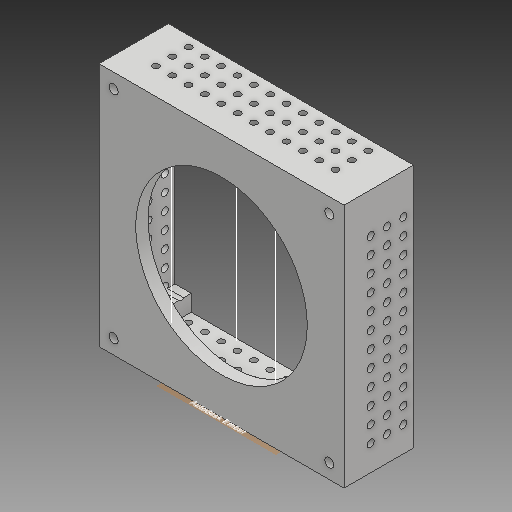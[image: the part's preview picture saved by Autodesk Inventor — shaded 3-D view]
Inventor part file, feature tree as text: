
AUTODESK INVENTOR PART (.ipt)
format: ipt  version: 2018 (Build 220112000, 112)  size: 539,648 bytes
history: native  units: mm
features: sketch x13, extrude x8, pattern_linear x3
ambient origin geometry x8: Origin, YZ Plane, XZ Plane, XY Plane, X Axis, Y Axis, Z Axis, Center Point
bodies: Solid1 (feature_tree)
feature tree (24):
  sketch  "Sketch1"  dims[d0=150.0mm d1=150.0mm]
  extrude  "Extrusion1"  Depth=150.0mm
  extrude  "Extrusion3"  Depth=4.0mm
  extrude  "Extrusion4"  Depth=10.0mm
  pattern_linear  "Rectangular Pattern1"  Count1=2 Spacing1=132.0mm
  extrude  "Extrusion5"  Depth=80.0mm
  pattern_linear  "Rectangular Pattern2"  Count1=8 Spacing1=0.0mm
  sketch  "Sketch9"  dims[d17=20.0mm d19=132.0mm d20=5.5mm d21=80.0mm d22=0.0mm]
  extrude  "Extrusion8"  Depth=132.0mm
  sketch  "Sketch11"  dims[d45=70.0mm d46=0.0mm d47=6.5mm d48=70.0mm d49=0.0mm]
  extrude  "Extrusion9"  Depth=6.5mm
  pattern_linear  "Rectangular Pattern5"  Count1=7 Spacing1=0.0mm
  extrude  "Extrusion10"  Depth=80.0mm
  sketch  "Sketch14"  dims[d57=12.5mm]
  sketch  "Sketch15"  dims[d58=70.0mm d59=0.0mm]
  extrude  "Extrusion11"  Depth=7.5mm TaperAngle=0.0deg
  sketch  "Sketch2"  dims[d2=7.5mm d3=0.0mm d7=4.0mm]
  sketch  "Sketch4"  dims[d8=35.0mm d9=0.0mm d10=10.0mm]
  sketch  "Sketch5"  dims[d11=10.0mm]
  sketch  "Sketch6"  dims[d12=35.0mm d13=0.0mm d14=20.0mm d16=132.0mm]
  sketch  "Sketch10"  dims[d23=20.0mm d25=132.0mm d26=20.0mm d28=132.0mm]
  sketch  "Sketch12"  dims[d50=30.0mm d52=10.0mm d53=80.0mm]
  sketch  "Sketch13"  dims[d54=7.5mm d55=70.0mm d56=0.0mm]
  sketch  "Sketch16"
